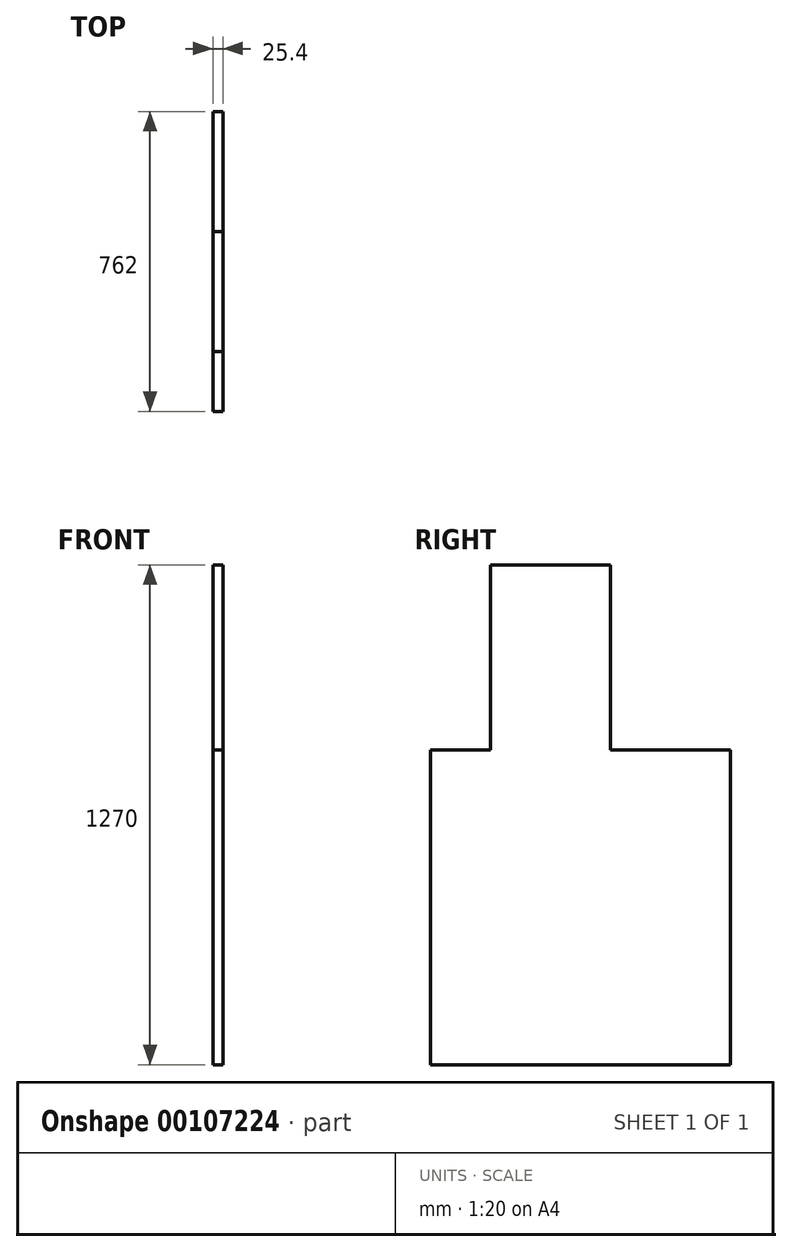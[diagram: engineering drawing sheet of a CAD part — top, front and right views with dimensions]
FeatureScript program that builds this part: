
annotation { "Feature Type Name" : "Feature", "Feature Type Description" : "" }
export const myFeature = defineFeature(function(context is Context, id is Id, definition is map)
    precondition{}
    {
        {
            var Q0;
            Q0=qCreatedBy(makeId("Right.planeOp"),FACE);
            var sketch = newSketch(context, id + "F0", { "sketchPlane" : qUnion([Q0])});
            skLineSegment(sketch, "E0.bottom", {"start": v(-990.6, 0) * mm, "end": v(-1752.6, 0) * mm});
            skLineSegment(sketch, "E0.top", {"start": v(-990.6, 800.1) * mm, "end": v(-1752.6, 800.1) * mm});
            skLineSegment(sketch, "E0.left", {"start": v(-990.6, 0) * mm, "end": v(-990.6, 800.1) * mm});
            skLineSegment(sketch, "E0.right", {"start": v(-1752.6, 0) * mm, "end": v(-1752.6, 800.1) * mm});
            skLineSegment(sketch, "E1", {"start": v(-990.6, 0) * mm, "end": v(0, 0) * mm, "construction": true});
            skLineSegment(sketch, "E2.bottom", {"start": v(-1600.2, 1270) * mm, "end": v(-1295.4, 1270) * mm});
            skLineSegment(sketch, "E2.top", {"start": v(-1600.2, 800.1) * mm, "end": v(-1295.4, 800.1) * mm});
            skLineSegment(sketch, "E2.left", {"start": v(-1600.2, 1270) * mm, "end": v(-1600.2, 800.1) * mm});
            skLineSegment(sketch, "E2.right", {"start": v(-1295.4, 1270) * mm, "end": v(-1295.4, 800.1) * mm});
            skSolve(sketch);
        }
        {
            var Q0;
            Q0=makeQuery(id+"F0.imprint","IMPRINT",FACE,{"disambiguationData":[TD([[makeQuery(id+"F0.imprint","IMPRINT",EDGE,{"derivedFrom":sQuery(id+"F0.wireOp",EDGE,"E0.bottom")}),-1.0]])]});
            var Q1;
            Q1=makeQuery(id+"F0.imprint","IMPRINT",FACE,{"disambiguationData":[TD([[makeQuery(id+"F0.imprint","IMPRINT",EDGE,{"derivedFrom":sQuery(id+"F0.wireOp",EDGE,"E2.bottom")}),-1.0]])]});
            extrude(context, id + "F1", {"entities" : qUnion([Q0, Q1]), "endBound" : BoundingType.SYMMETRIC, "depth" : 25.4 * mm});
        }
    });
